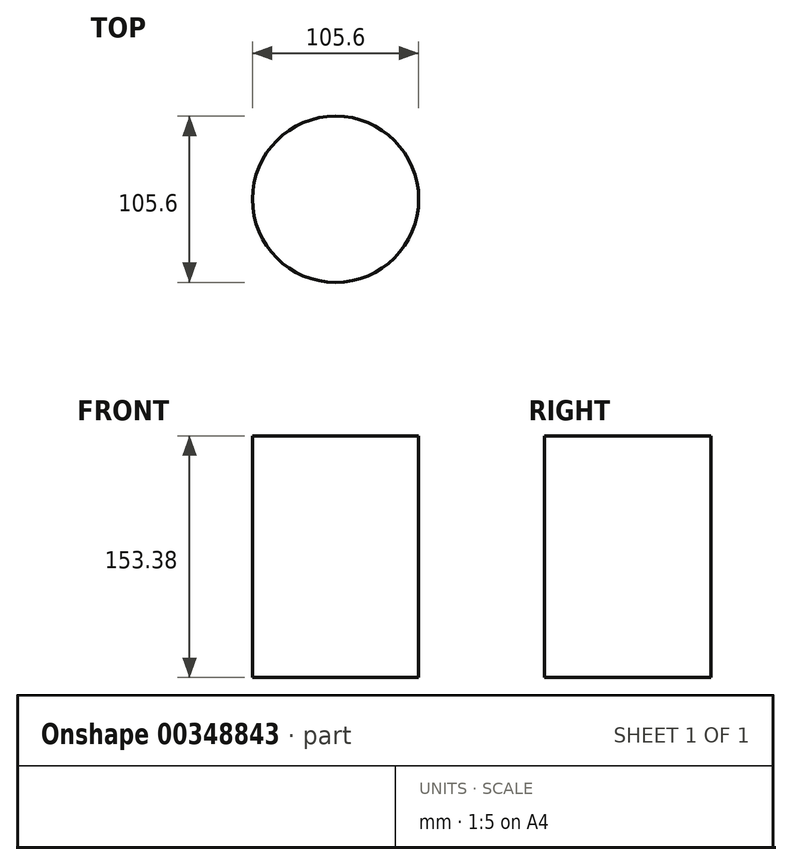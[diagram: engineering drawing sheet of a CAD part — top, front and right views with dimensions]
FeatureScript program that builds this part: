
annotation { "Feature Type Name" : "Feature", "Feature Type Description" : "" }
export const myFeature = defineFeature(function(context is Context, id is Id, definition is map)
    precondition{}
    {
        {
            var Q0;
            Q0=qCreatedBy(makeId("Front.planeOp"),FACE);
            var sketch = newSketch(context, id + "F0", { "sketchPlane" : qUnion([Q0])});
            skLineSegment(sketch, "E0.bottom", {"start": v(0, 73.67) * mm, "end": v(-52.8, 73.67) * mm});
            skLineSegment(sketch, "E0.top", {"start": v(0, -79.7) * mm, "end": v(-52.8, -79.7) * mm});
            skLineSegment(sketch, "E0.left", {"start": v(0, 73.67) * mm, "end": v(0, -79.7) * mm});
            skLineSegment(sketch, "E0.right", {"start": v(-52.8, 73.67) * mm, "end": v(-52.8, -79.7) * mm});
            skLineSegment(sketch, "E1", {"start": v(0, 115.42) * mm, "end": v(0, -158.1) * mm, "construction": true});
            skSolve(sketch);
        }
        {
            var Q0;
            Q0=makeQuery(id+"F0.imprint","IMPRINT",FACE,{"disambiguationData":[TD([[makeQuery(id+"F0.imprint","IMPRINT",EDGE,{"derivedFrom":sQuery(id+"F0.wireOp",EDGE,"E0.bottom")}),1.0]])]});
            var Q1;
            Q1=sQuery(id+"F0.wireOp",EDGE,"E1");
            revolve(context, id + "F1", {"entities" : qUnion([Q0]), "axis" : qUnion([Q1]), "revolveType" : RevolveType.FULL});
        }
    });
